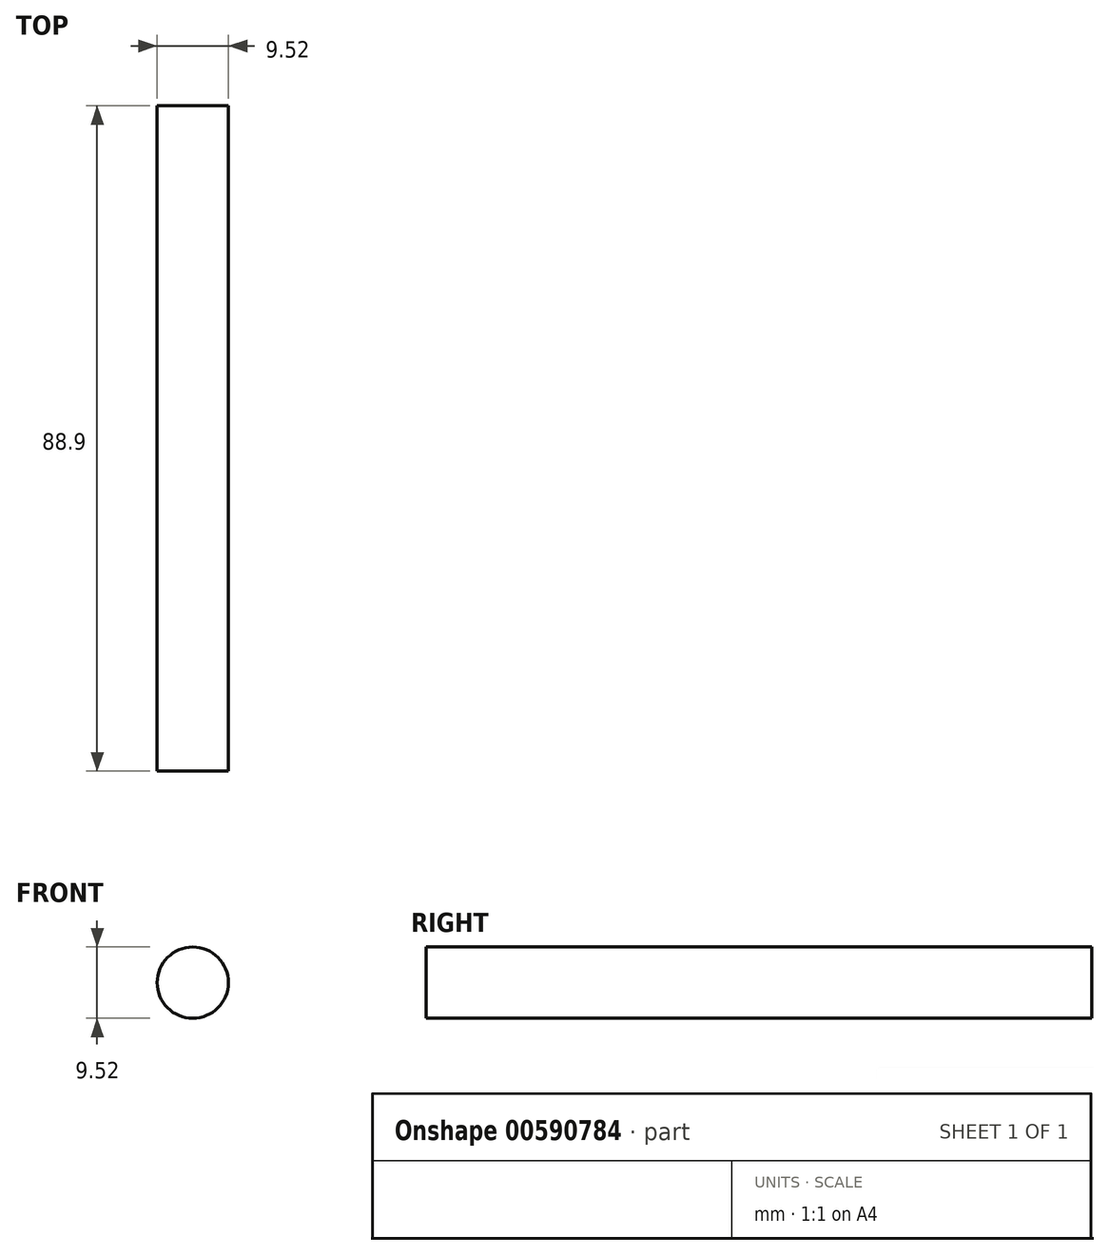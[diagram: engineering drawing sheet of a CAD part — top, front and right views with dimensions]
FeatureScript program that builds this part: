
annotation { "Feature Type Name" : "Feature", "Feature Type Description" : "" }
export const myFeature = defineFeature(function(context is Context, id is Id, definition is map)
    precondition{}
    {
        {
            var Q0;
            Q0=qCreatedBy(makeId("Front.planeOp"),FACE);
            var sketch = newSketch(context, id + "F0", { "sketchPlane" : qUnion([Q0])});
            skCircle(sketch, "E0", {"center": v(0, 0) * mm, "radius": 4.76 * mm});
            skSolve(sketch);
        }
        {
            var Q0;
            Q0 = qSketchRegion(id + "F0", true);
            extrude(context, id + "F1", {"entities" : qUnion([Q0]), "depth" : 88.9 * mm, "offsetDistance" : 25.4 * mm});
        }
    });
